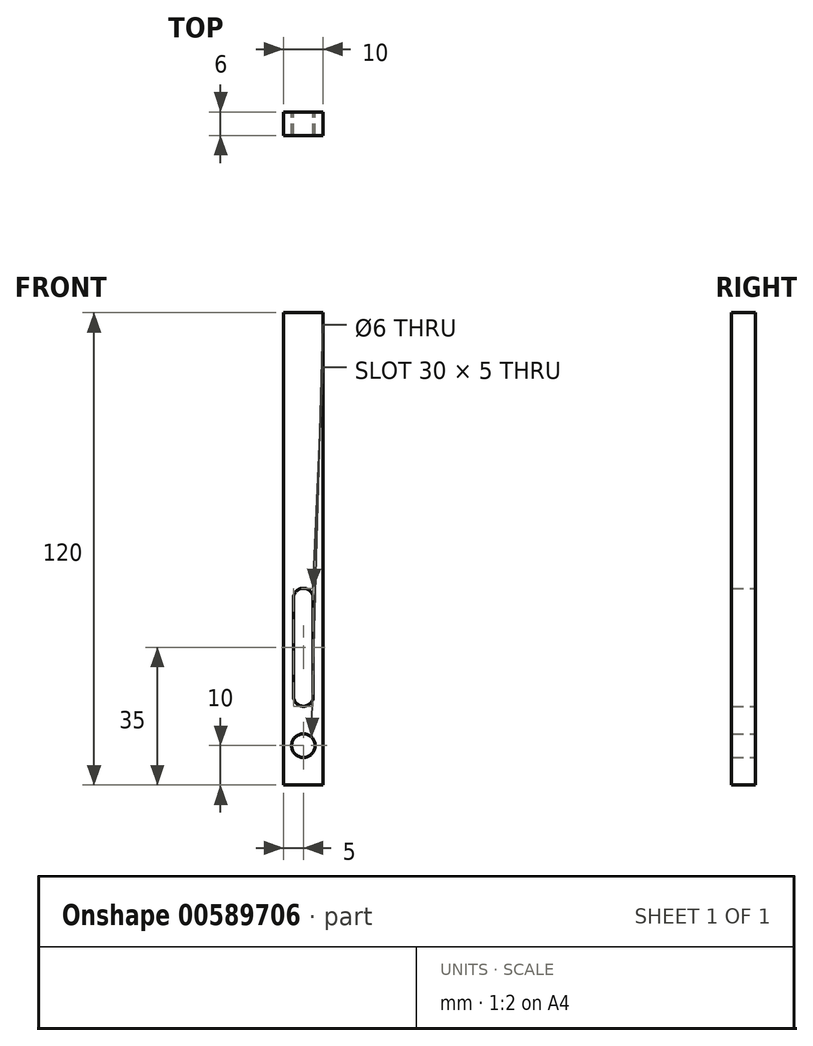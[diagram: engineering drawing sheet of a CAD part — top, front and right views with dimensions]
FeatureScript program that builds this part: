
annotation { "Feature Type Name" : "Feature", "Feature Type Description" : "" }
export const myFeature = defineFeature(function(context is Context, id is Id, definition is map)
    precondition{}
    {
        {
            var Q0;
            Q0=qCreatedBy(makeId("Front.planeOp"),FACE);
            var sketch = newSketch(context, id + "F0", { "sketchPlane" : qUnion([Q0])});
            skLineSegment(sketch, "E0.bottom", {"start": v(0, 0) * mm, "end": v(-5, 0) * mm});
            skLineSegment(sketch, "E0.top", {"start": v(0, 120) * mm, "end": v(-5, 120) * mm});
            skLineSegment(sketch, "E0.left", {"start": v(0, 0) * mm, "end": v(0, 120) * mm, "construction": true});
            skLineSegment(sketch, "E0.right", {"start": v(-5, 0) * mm, "end": v(-5, 120) * mm});
            skLineSegment(sketch, "E1.MirrorCS", {"start": v(0, 0) * mm, "end": v(5, 0) * mm});
            skLineSegment(sketch, "E2.MirrorCS", {"start": v(5, 0) * mm, "end": v(5, 120) * mm});
            skLineSegment(sketch, "E3.MirrorCS", {"start": v(0, 120) * mm, "end": v(5, 120) * mm});
            skCircle(sketch, "E4", {"center": v(0, 10) * mm, "radius": 3 * mm});
            skLineSegment(sketch, "E5.bottom", {"start": v(2.5, 47.5) * mm, "end": v(-2.5, 47.5) * mm});
            skLineSegment(sketch, "E5.top", {"start": v(2.5, 22.5) * mm, "end": v(-2.5, 22.5) * mm});
            skLineSegment(sketch, "E5.left", {"start": v(2.5, 47.5) * mm, "end": v(2.5, 22.5) * mm});
            skLineSegment(sketch, "E5.right", {"start": v(-2.5, 47.5) * mm, "end": v(-2.5, 22.5) * mm});
            skPoint(sketch, "E5.middle", {"position": v(0, 35) * mm});
            skArc(sketch, "E6", {"start": v(2.5, 47.5) * mm, "mid": v(0, 50) * mm, "end": v(-2.5, 47.5) * mm});
            skArc(sketch, "E7", {"start": v(-2.5, 22.5) * mm, "mid": v(0, 20) * mm, "end": v(2.5, 22.5) * mm});
            skSolve(sketch);
        }
        {
            var Q0;
            Q0=makeQuery(id+"F0.imprint","IMPRINT",FACE,{"disambiguationData":[TD([[makeQuery(id+"F0.imprint","IMPRINT",EDGE,{"derivedFrom":sQuery(id+"F0.wireOp",EDGE,"E0.bottom")}),-1.0]])]});
            extrude(context, id + "F1", {"entities" : qUnion([Q0]), "depth" : 6 * mm, "offsetDistance" : 25 * mm});
        }
    });
